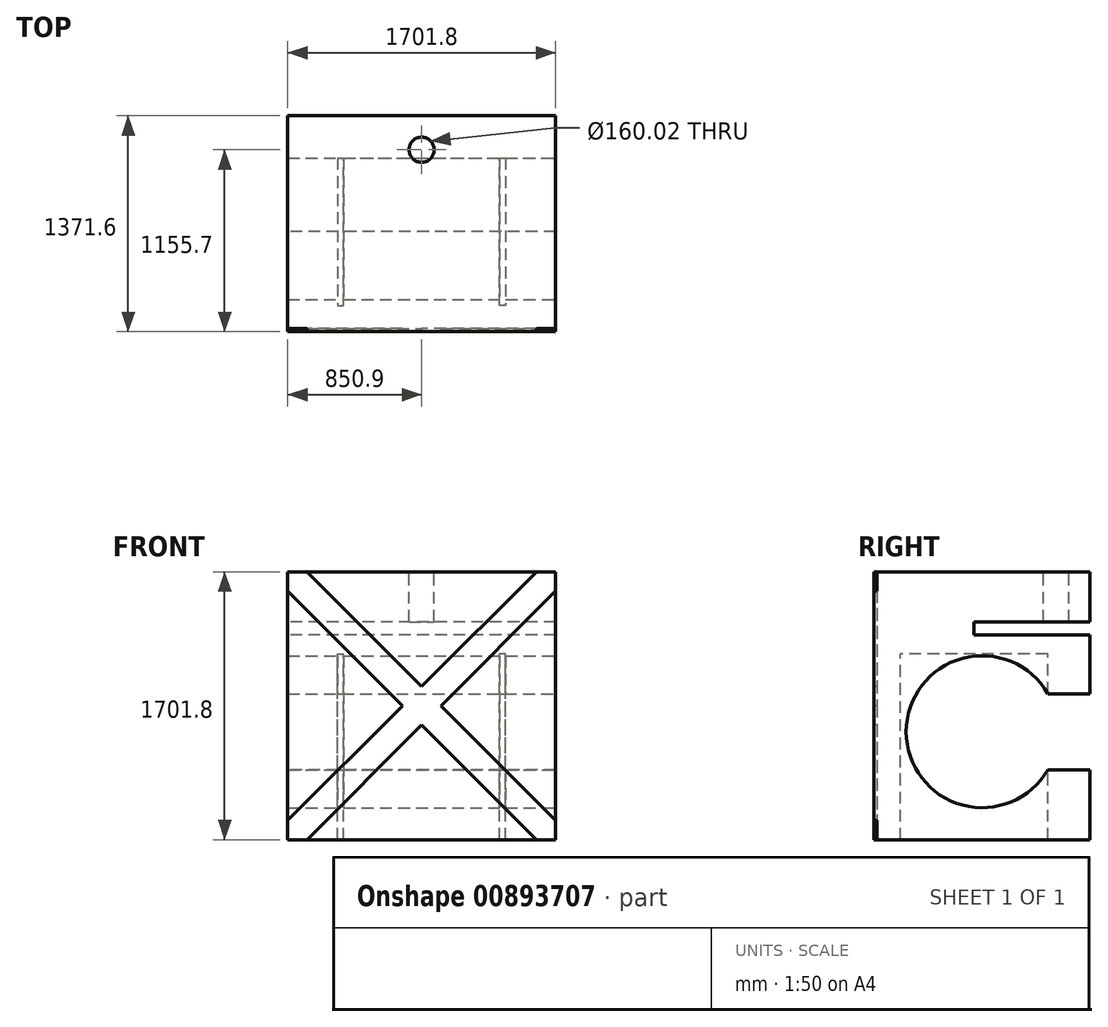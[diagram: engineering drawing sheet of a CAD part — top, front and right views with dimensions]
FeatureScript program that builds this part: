
annotation { "Feature Type Name" : "Feature", "Feature Type Description" : "" }
export const myFeature = defineFeature(function(context is Context, id is Id, definition is map)
    precondition{}
    {
        {
            var Q0;
            Q0=qCreatedBy(makeId("Front.planeOp"),FACE);
            var sketch = newSketch(context, id + "F0", { "sketchPlane" : qUnion([Q0])});
            skLineSegment(sketch, "E0.bottom", {"start": v(-850.9, 850.9) * mm, "end": v(850.9, 850.9) * mm});
            skLineSegment(sketch, "E0.top", {"start": v(-850.9, -850.9) * mm, "end": v(850.9, -850.9) * mm});
            skLineSegment(sketch, "E0.left", {"start": v(-850.9, 850.9) * mm, "end": v(-850.9, -850.9) * mm});
            skLineSegment(sketch, "E0.right", {"start": v(850.9, 850.9) * mm, "end": v(850.9, -850.9) * mm});
            skPoint(sketch, "E0.middle", {"position": v(0, 0) * mm});
            skSolve(sketch);
        }
        {
            var Q0;
            Q0 = qSketchRegion(id + "F0", true);
            extrude(context, id + "F1", {"entities" : qUnion([Q0]), "endBound" : BoundingType.SYMMETRIC, "depth" : 1371.6 * mm, "offsetDistance" : 25.4 * mm});
        }
        {
            var Q0;
            Q0=makeQuery(id+"F1.opExtrude","CAP_FACE",FACE,{"disambiguationData":[OSD([sQuery(id+"F0.wireOp",EDGE,"E0.bottom"),sQuery(id+"F0.wireOp",EDGE,"E0.top"),sQuery(id+"F0.wireOp",EDGE,"E0.left"),sQuery(id+"F0.wireOp",EDGE,"E0.right")])],"isStart":false});
            var sketch = newSketch(context, id + "F2", { "sketchPlane" : qUnion([Q0])});
            skLineSegment(sketch, "E1", {"start": v(728.98, 850.9) * mm, "end": v(-850.9, -728.98) * mm});
            skLineSegment(sketch, "E2", {"start": v(850.9, 728.98) * mm, "end": v(-728.98, -850.9) * mm});
            skLineSegment(sketch, "E3", {"start": v(-728.98, 850.9) * mm, "end": v(850.9, -728.98) * mm});
            skLineSegment(sketch, "E4", {"start": v(-850.9, 728.98) * mm, "end": v(728.98, -850.9) * mm});
            skSolve(sketch);
        }
        {
            var Q0;
            Q0 = qSketchRegion(id + "F2", true);
            var Q1;
            {var subQ3=sQuery(id+"F2.wireOp",EDGE,"E3");var subQ5=sQuery(id+"F2.wireOp",EDGE,"E1");var subQ6=makeQuery(id+"F2.imprint","INTERSECT",VERTEX,{"derivedFrom":[subQ5,subQ3]});Q1=makeQuery(id+"F2.imprint","IMPRINT",FACE,{"disambiguationData":[TD([[makeQuery(id+"F2.imprint","IMPRINT",EDGE,{"disambiguationData":[TD([[subQ6,-1.0]])],"derivedFrom":subQ5}),-1.0]])]});}
            var Q2;
            {var subQ1=sQuery(id+"F2.wireOp",EDGE,"E1");var subQ6=makeQuery(id+"F1.opExtrude","CAP_EDGE",EDGE,{"disambiguationData":[OSD([sQuery(id+"F0.wireOp",EDGE,"E0.bottom")])],"isStart":false});var subQ8=makeQuery(id+"F2.imprint","INTERSECT",VERTEX,{"derivedFrom":[subQ6,subQ1]});Q2=makeQuery(id+"F2.imprint","IMPRINT",FACE,{"disambiguationData":[TD([[makeQuery(id+"F2.imprint","IMPRINT",EDGE,{"disambiguationData":[TD([[subQ8,-1.0]])],"derivedFrom":subQ1}),1.0]])]});}
            var Q3;
            {var subQ5=sQuery(id+"F2.wireOp",EDGE,"E2");var subQ7=sQuery(id+"F2.wireOp",EDGE,"E3");var subQ9=makeQuery(id+"F2.imprint","INTERSECT",VERTEX,{"derivedFrom":[subQ5,subQ7]});Q3=makeQuery(id+"F2.imprint","IMPRINT",FACE,{"disambiguationData":[TD([[makeQuery(id+"F2.imprint","IMPRINT",EDGE,{"disambiguationData":[TD([[subQ9,-1.0]])],"derivedFrom":subQ5}),1.0]])]});}
            var Q4;
            {var subQ0=makeQuery(id+"F1.opExtrude","CAP_EDGE",EDGE,{"disambiguationData":[OSD([sQuery(id+"F0.wireOp",EDGE,"E0.left")])],"isStart":false});var subQ6=sQuery(id+"F2.wireOp",EDGE,"E1");var subQ9=makeQuery(id+"F2.imprint","INTERSECT",VERTEX,{"derivedFrom":[subQ0,subQ6]});Q4=makeQuery(id+"F2.imprint","IMPRINT",FACE,{"disambiguationData":[TD([[makeQuery(id+"F2.imprint","IMPRINT",EDGE,{"disambiguationData":[TD([[subQ9,1.0]])],"derivedFrom":subQ6}),1.0]])]});}
            extrude(context, id + "F3", {"entities" : qUnion([Q0, Q1, Q2, Q3, Q4]), "operationType" : NewBodyOperationType.REMOVE, "endBound" : BoundingType.SYMMETRIC, "oppositeDirection" : true, "depth" : 38.1 * mm, "offsetDistance" : 25.4 * mm});
        }
        {
            var Q0;
            Q0=makeQuery(id+"F1.opExtrude","SWEPT_FACE",FACE,{"disambiguationData":[OSD([sQuery(id+"F0.wireOp",EDGE,"E0.bottom")])]});
            var sketch = newSketch(context, id + "F4", { "sketchPlane" : qUnion([Q0])});
            skCircle(sketch, "E5", {"center": v(0, 469.9) * mm, "radius": 80.01 * mm});
            skSolve(sketch);
        }
        {
            var Q0;
            Q0 = qSketchRegion(id + "F4", true);
            extrude(context, id + "F5", {"entities" : qUnion([Q0]), "operationType" : NewBodyOperationType.REMOVE, "oppositeDirection" : true, "depth" : 381 * mm, "offsetDistance" : 25.4 * mm});
        }
        {
            var Q0;
            Q0=makeQuery(id+"F1.opExtrude","SWEPT_FACE",FACE,{"disambiguationData":[OSD([sQuery(id+"F0.wireOp",EDGE,"E0.right")])]});
            var sketch = newSketch(context, id + "F6", { "sketchPlane" : qUnion([Q0])});
            skLineSegment(sketch, "E6", {"start": v(685.8, 533.4) * mm, "end": v(-50.8, 533.4) * mm});
            skLineSegment(sketch, "E7", {"start": v(-50.8, 533.4) * mm, "end": v(-50.8, 449.58) * mm});
            skLineSegment(sketch, "E8", {"start": v(-50.8, 449.58) * mm, "end": v(685.8, 449.58) * mm});
            skSolve(sketch);
        }
        {
            var Q0;
            {var subQ0=sQuery(id+"F6.wireOp",EDGE,"E6");Q0=makeQuery(id+"F6.imprint","IMPRINT",FACE,{"disambiguationData":[TD([[makeQuery(id+"F6.imprint","IMPRINT",EDGE,{"derivedFrom":subQ0}),1.0]])]});}
            extrude(context, id + "F7", {"entities" : qUnion([Q0]), "operationType" : NewBodyOperationType.REMOVE, "endBound" : BoundingType.SYMMETRIC, "depth" : 5080 * mm, "offsetDistance" : 25.4 * mm});
        }
        {
            var Q0;
            Q0=makeQuery(id+"F1.opExtrude","SWEPT_FACE",FACE,{"disambiguationData":[OSD([sQuery(id+"F0.wireOp",EDGE,"E0.right")])]});
            var sketch = newSketch(context, id + "F8", { "sketchPlane" : qUnion([Q0])});
            skCircle(sketch, "E9", {"center": v(0, -164.73) * mm, "radius": 482.6 * mm});
            skLineSegment(sketch, "E10", {"start": v(685.8, 76.57) * mm, "end": v(384.07, 76.57) * mm});
            skLineSegment(sketch, "E11", {"start": v(686.1, -406.03) * mm, "end": v(355.02, -406.03) * mm});
            skLineSegment(sketch, "E12", {"start": v(685.8, 76.57) * mm, "end": v(686.1, -406.03) * mm});
            skLineSegment(sketch, "E13", {"start": v(685.8, -164.73) * mm, "end": v(685.8, -406.03) * mm});
            skLineSegment(sketch, "E14", {"start": v(685.8, -406.03) * mm, "end": v(685.8, 76.57) * mm});
            skSolve(sketch);
        }
        {
            var Q0;
            Q0 = qSketchRegion(id + "F8", true);
            extrude(context, id + "F9", {"entities" : qUnion([Q0]), "operationType" : NewBodyOperationType.REMOVE, "oppositeDirection" : true, "depth" : 5080 * mm, "offsetDistance" : 25.4 * mm});
        }
        {
            var Q0;
            Q0=makeQuery(id+"F9.boolean.opBoolean","COPY",FACE,{"derivedFrom":makeQuery(id+"F9.opExtrude","SWEPT_FACE",FACE,{"disambiguationData":[OSD([sQuery(id+"F8.wireOp",EDGE,"E11")])]})});
            var sketch = newSketch(context, id + "F10", { "sketchPlane" : qUnion([Q0])});
            skLineSegment(sketch, "E15", {"start": v(850.9, 417.94) * mm, "end": v(533.4, 417.94) * mm});
            skLineSegment(sketch, "E16", {"start": v(533.4, 417.94) * mm, "end": v(533.4, -519.74) * mm});
            skLineSegment(sketch, "E17", {"start": v(533.4, -519.74) * mm, "end": v(495.3, -519.74) * mm});
            skLineSegment(sketch, "E18", {"start": v(495.3, -519.74) * mm, "end": v(495.3, 417.94) * mm});
            skLineSegment(sketch, "E19", {"start": v(495.3, 417.94) * mm, "end": v(533.4, 417.94) * mm});
            skLineSegment(sketch, "E20.MirrorCS", {"start": v(-533.4, 417.94) * mm, "end": v(-533.4, -519.74) * mm});
            skLineSegment(sketch, "E21.MirrorCS", {"start": v(-495.3, -519.74) * mm, "end": v(-495.3, 417.94) * mm});
            skLineSegment(sketch, "E22.MirrorCS", {"start": v(-533.4, -519.74) * mm, "end": v(-495.3, -519.74) * mm});
            skLineSegment(sketch, "E23.MirrorCS", {"start": v(-495.3, 417.94) * mm, "end": v(-533.4, 417.94) * mm});
            skSolve(sketch);
        }
        {
            var Q0;
            Q0 = qSketchRegion(id + "F10", true);
            extrude(context, id + "F11", {"entities" : qUnion([Q0]), "operationType" : NewBodyOperationType.REMOVE, "endBound" : BoundingType.SYMMETRIC, "oppositeDirection" : true, "depth" : 1473.2 * mm, "offsetDistance" : 25.4 * mm});
        }
    });
